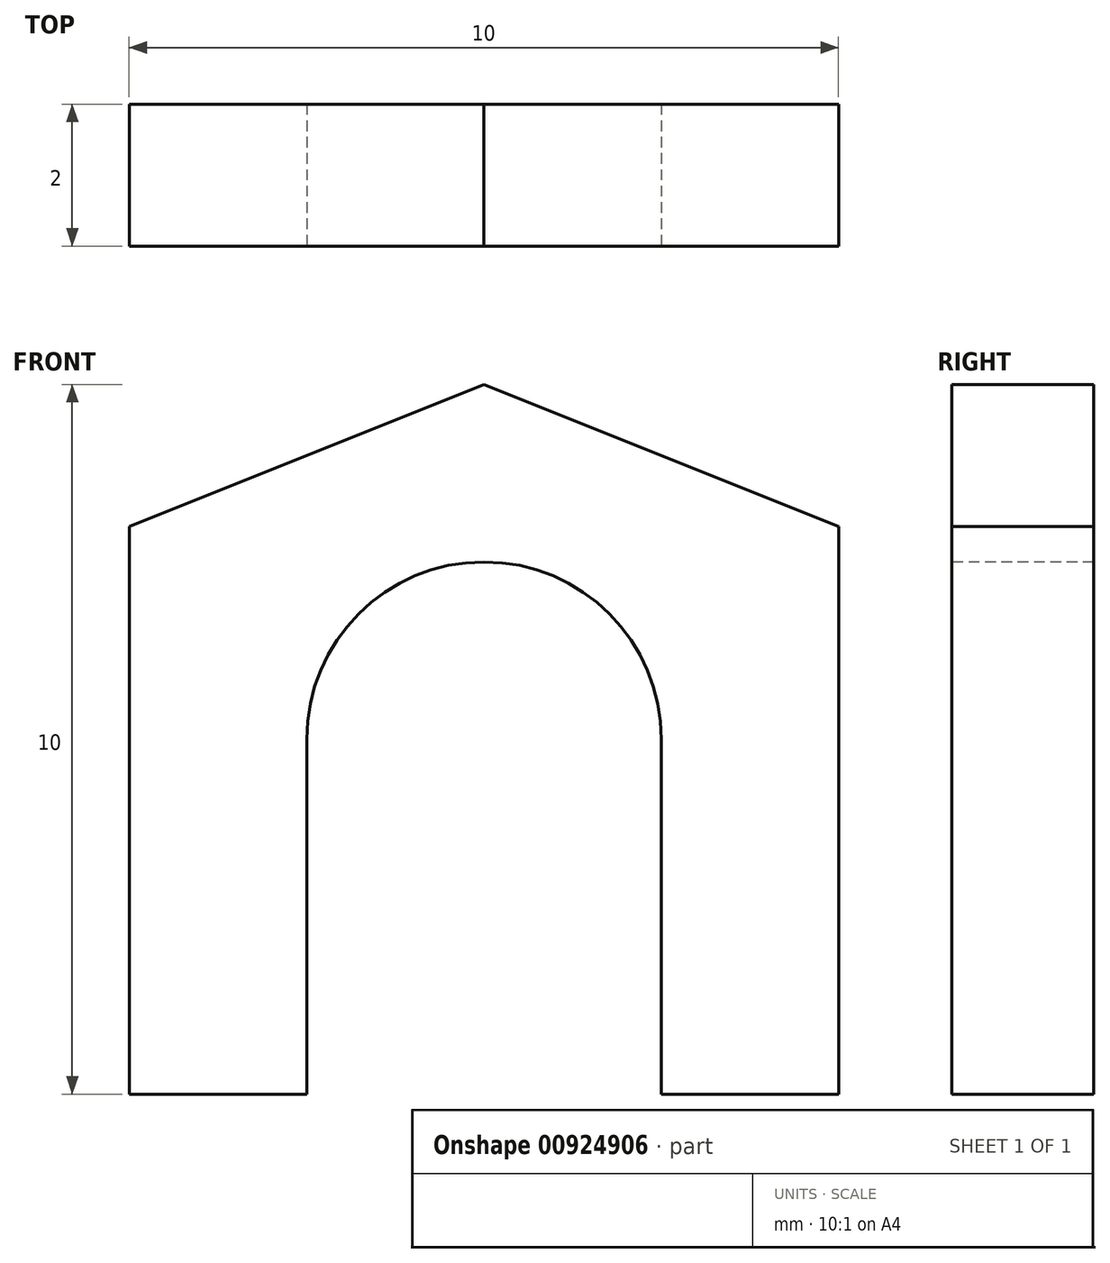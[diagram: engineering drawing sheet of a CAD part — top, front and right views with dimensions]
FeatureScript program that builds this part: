
annotation { "Feature Type Name" : "Feature", "Feature Type Description" : "" }
export const myFeature = defineFeature(function(context is Context, id is Id, definition is map)
    precondition{}
    {
        {
            var Q0;
            Q0=qCreatedBy(makeId("Front.planeOp"),FACE);
            var sketch = newSketch(context, id + "F0", { "sketchPlane" : qUnion([Q0])});
            skLineSegment(sketch, "E0.top", {"start": v(-42.92, 0) * mm, "end": v(-32.92, 0) * mm});
            skLineSegment(sketch, "E0.left", {"start": v(-42.92, 8) * mm, "end": v(-42.92, 0) * mm});
            skLineSegment(sketch, "E0.right", {"start": v(-32.92, 8) * mm, "end": v(-32.92, 0) * mm});
            skLineSegment(sketch, "E1", {"start": v(-42.92, 8) * mm, "end": v(-37.92, 10) * mm});
            skLineSegment(sketch, "E2", {"start": v(-37.92, 10) * mm, "end": v(-32.92, 8) * mm});
            skLineSegment(sketch, "E3.top", {"start": v(-28.01, -1.8) * mm, "end": v(-18.01, -1.8) * mm});
            skLineSegment(sketch, "E3.left", {"start": v(-28.01, 6.2) * mm, "end": v(-28.01, -1.8) * mm});
            skLineSegment(sketch, "E3.right", {"start": v(-18.01, 6.2) * mm, "end": v(-18.01, -1.8) * mm});
            skLineSegment(sketch, "E4", {"start": v(-28.01, 6.2) * mm, "end": v(-23.01, 8.2) * mm});
            skLineSegment(sketch, "E5", {"start": v(-23.01, 8.2) * mm, "end": v(-18.01, 6.2) * mm});
            skSolve(sketch);
        }
        {
            var Q0;
            Q0=makeQuery(id+"F0.imprint","IMPRINT",FACE,{"disambiguationData":[TD([[makeQuery(id+"F0.imprint","IMPRINT",EDGE,{"derivedFrom":sQuery(id+"F0.wireOp",EDGE,"E0.top")}),1.0]])]});
            extrude(context, id + "F1", {"entities" : qUnion([Q0]), "depth" : 2 * mm, "offsetDistance" : 25 * mm});
        }
        {
            var Q0;
            Q0=makeQuery(id+"F1.opExtrude","CAP_FACE",FACE,{"disambiguationData":[OSD([sQuery(id+"F0.wireOp",EDGE,"E0.top"),sQuery(id+"F0.wireOp",EDGE,"E0.left"),sQuery(id+"F0.wireOp",EDGE,"E0.right"),sQuery(id+"F0.wireOp",EDGE,"E1"),sQuery(id+"F0.wireOp",EDGE,"E2")])],"isStart":false});
            var sketch = newSketch(context, id + "F2", { "sketchPlane" : qUnion([Q0])});
            skLineSegment(sketch, "E6.left", {"start": v(-40.42, 5) * mm, "end": v(-40.42, 0) * mm});
            skLineSegment(sketch, "E6.right", {"start": v(-35.42, 5) * mm, "end": v(-35.42, 0) * mm});
            skArc(sketch, "E7", {"start": v(-35.42, 5) * mm, "mid": v(-37.92, 7.5) * mm, "end": v(-40.42, 5) * mm});
            skLineSegment(sketch, "E8", {"start": v(-37.92, 0) * mm, "end": v(-40.42, 0) * mm});
            skLineSegment(sketch, "E9", {"start": v(-40.42, 0) * mm, "end": v(-40.42, -2.82) * mm});
            skSolve(sketch);
        }
        {
            var Q0;
            Q0=makeQuery(id+"F2.imprint","IMPRINT",FACE,{"disambiguationData":[TD([[makeQuery(id+"F2.imprint","IMPRINT",EDGE,{"derivedFrom":sQuery(id+"F2.wireOp",EDGE,"E6.left")}),1.0]])]});
            extrude(context, id + "F3", {"entities" : qUnion([Q0]), "operationType" : NewBodyOperationType.REMOVE, "oppositeDirection" : true, "depth" : 25 * mm, "offsetDistance" : 25 * mm});
        }
    });
